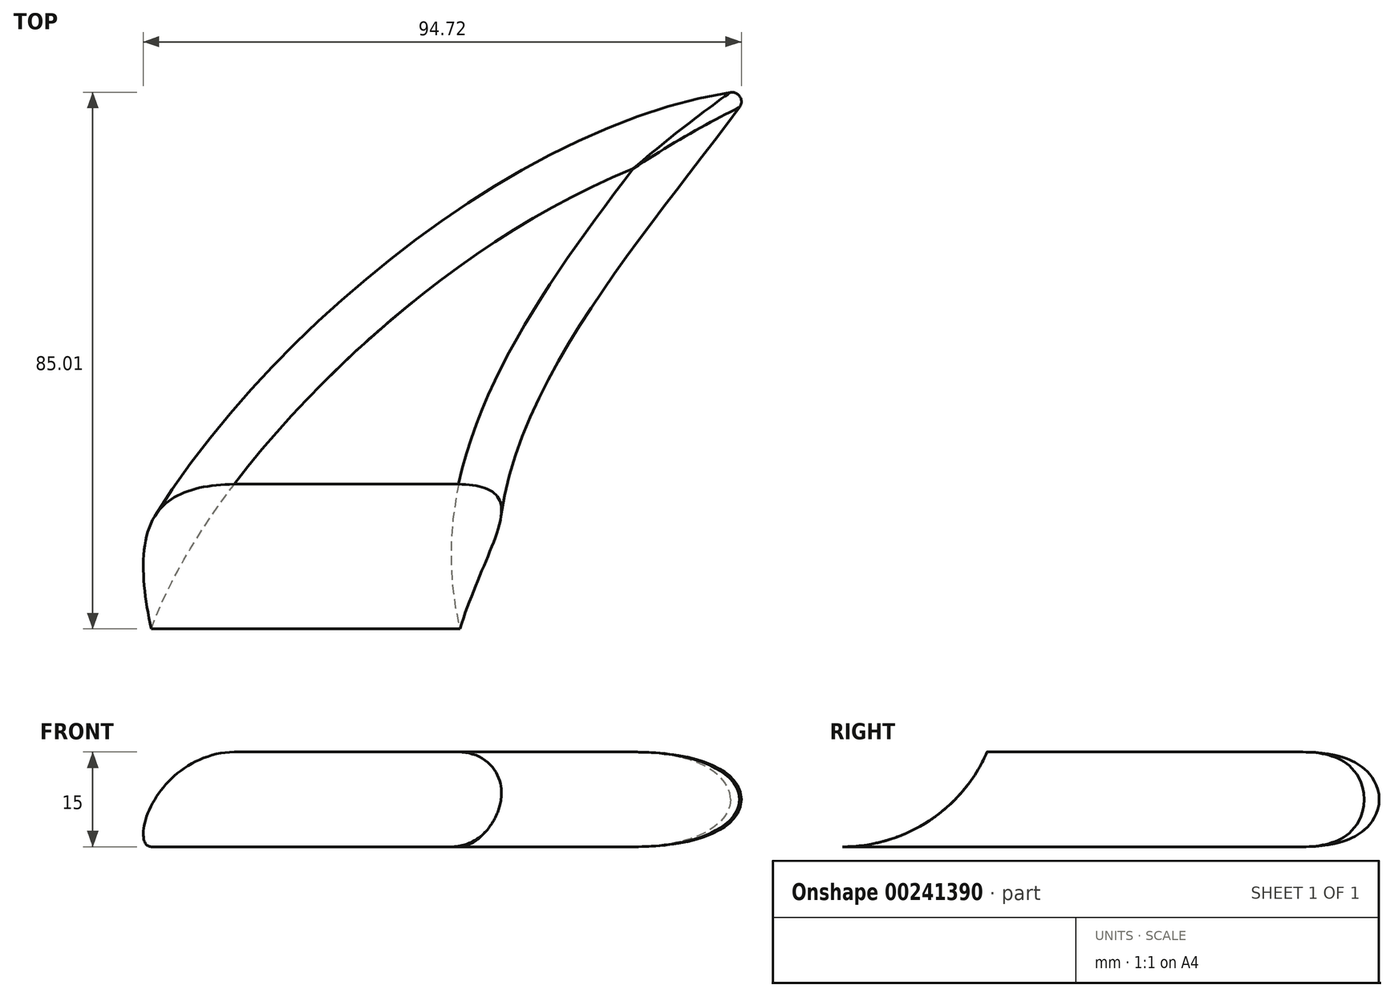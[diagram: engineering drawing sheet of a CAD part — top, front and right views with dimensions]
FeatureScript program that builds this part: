
annotation { "Feature Type Name" : "Feature", "Feature Type Description" : "" }
export const myFeature = defineFeature(function(context is Context, id is Id, definition is map)
    precondition{}
    {
        {
            var Q0;
            Q0=qCreatedBy(makeId("Top.planeOp"),FACE);
            var sketch = newSketch(context, id + "F0", { "sketchPlane" : qUnion([Q0])});
            skLineSegment(sketch, "E0", {"start": v(-26.94, 0) * mm, "end": v(37.6, 0) * mm});
            skPoint(sketch, "E1", {"position": v(76.2, 85.43) * mm});
            skFitSpline(sketch, "E2", {"points": [v(-26.94, 0) * mm, v(76.2, 85.43) * mm], "startDerivative": vector(30.2, 99.47) * mm, "endDerivative": vector(123.98, 11.95) * mm});
            skFitSpline(sketch, "E3", {"points": [v(37.6, 0) * mm, v(76.2, 85.43) * mm], "startDerivative": vector(-26.1, 89) * mm, "endDerivative": vector(61.24, 83.65) * mm});
            skSolve(sketch);
        }
        {
            var Q0;
            Q0 = qSketchRegion(id + "F0", true);
            extrude(context, id + "F1", {"entities" : qUnion([Q0]), "depth" : 15 * mm});
        }
        {
            var Q0;
            Q0=makeQuery(id+"F1.opExtrude","SWEPT_EDGE",EDGE,{"disambiguationData":[OSD([sQuery(id+"F0.wireOp",EDGE,"E2"),sQuery(id+"F0.wireOp",EDGE,"E3")])]});
            fillet(context, id + "F2", {"entities" : qUnion([Q0]), "radius" : 1.5 * mm, "tangentPropagation" : true, "allowEdgeOverflow" : false});
        }
        {
            var Q0;
            Q0=makeQuery(id+"F1.opExtrude","CAP_EDGE",EDGE,{"disambiguationData":[OSD([sQuery(id+"F0.wireOp",EDGE,"E2")])],"isStart":false});
            var Q1;
            Q1=makeQuery(id+"F1.opExtrude","CAP_EDGE",EDGE,{"disambiguationData":[OSD([sQuery(id+"F0.wireOp",EDGE,"E2")])],"isStart":true});
            fillet(context, id + "F3", {"entities" : qUnion([Q0, Q1]), "radius" : 7.5 * mm, "tangentPropagation" : true, "allowEdgeOverflow" : false});
        }
        {
            var Q0;
            Q0=qCreatedBy(makeId("Right.planeOp"),FACE);
            var sketch = newSketch(context, id + "F4", { "sketchPlane" : qUnion([Q0])});
            skLineSegment(sketch, "E4.bottom", {"start": v(-135.79, 0) * mm, "end": v(0, 0) * mm});
            skLineSegment(sketch, "E4.top", {"start": v(-135.79, 50) * mm, "end": v(25, 50) * mm});
            skLineSegment(sketch, "E4.left", {"start": v(-135.79, 0) * mm, "end": v(-135.79, 50) * mm});
            skLineSegment(sketch, "E4.right", {"start": v(25, 25) * mm, "end": v(25, 50) * mm});
            skPoint(sketch, "E5.visualSharp", {"position": v(25, 0) * mm});
            skArc(sketch, "E5.filletArc", {"start": v(0, 0) * mm, "mid": v(17.68, 7.32) * mm, "end": v(25, 25) * mm});
            skSolve(sketch);
        }
        {
            var Q0;
            Q0 = qSketchRegion(id + "F4", true);
            extrude(context, id + "F5", {"entities" : qUnion([Q0]), "operationType" : NewBodyOperationType.REMOVE, "endBound" : BoundingType.SYMMETRIC, "oppositeDirection" : true, "depth" : 100 * mm});
        }
    });
